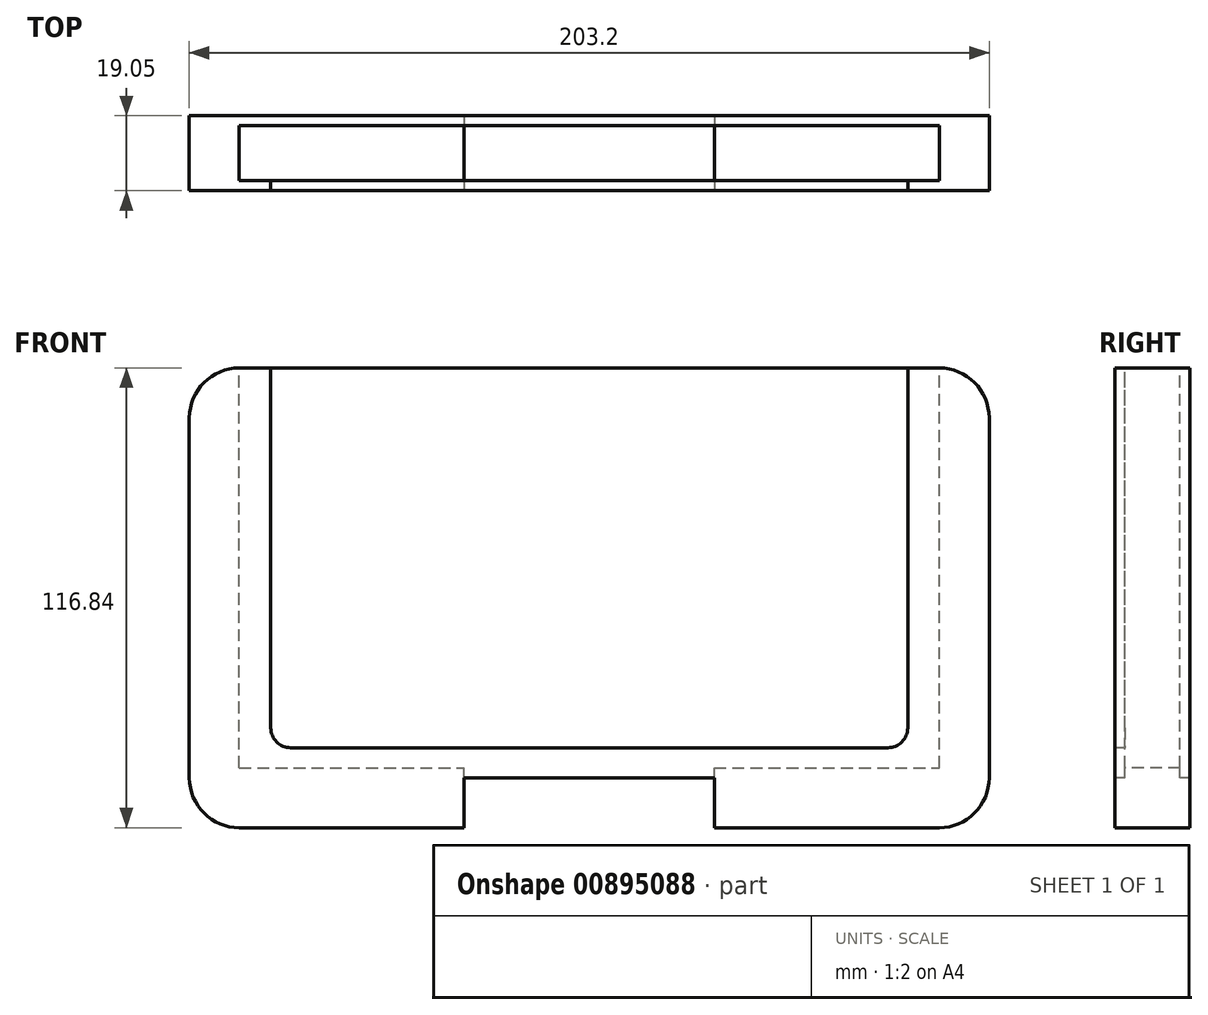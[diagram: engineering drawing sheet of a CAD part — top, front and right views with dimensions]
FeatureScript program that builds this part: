
annotation { "Feature Type Name" : "Feature", "Feature Type Description" : "" }
export const myFeature = defineFeature(function(context is Context, id is Id, definition is map)
    precondition{}
    {
        {
            var Q0;
            Q0=qCreatedBy(makeId("Front.planeOp"),FACE);
            var sketch = newSketch(context, id + "F0", { "sketchPlane" : qUnion([Q0])});
            skLineSegment(sketch, "E0.bottom", {"start": v(0, 0) * mm, "end": v(203.2, 0) * mm});
            skLineSegment(sketch, "E0.top", {"start": v(0, 116.84) * mm, "end": v(203.2, 116.84) * mm});
            skLineSegment(sketch, "E0.left", {"start": v(0, 0) * mm, "end": v(0, 116.84) * mm});
            skLineSegment(sketch, "E0.right", {"start": v(203.2, 0) * mm, "end": v(203.2, 116.84) * mm});
            skSolve(sketch);
        }
        {
            var Q0;
            Q0=makeQuery(id+"F0.imprint","IMPRINT",FACE,{"disambiguationData":[TD([[makeQuery(id+"F0.imprint","IMPRINT",EDGE,{"derivedFrom":sQuery(id+"F0.wireOp",EDGE,"E0.bottom")}),1.0]])]});
            extrude(context, id + "F1", {"entities" : qUnion([Q0]), "depth" : 19.05 * mm, "offsetDistance" : 25.4 * mm});
        }
        {
            var Q0;
            Q0=makeQuery(id+"F1.opExtrude","SWEPT_FACE",FACE,{"disambiguationData":[OSD([sQuery(id+"F0.wireOp",EDGE,"E0.top")])]});
            var sketch = newSketch(context, id + "F2", { "sketchPlane" : qUnion([Q0])});
            skLineSegment(sketch, "E1.bottom", {"start": v(12.7, -2.54) * mm, "end": v(190.5, -2.54) * mm});
            skLineSegment(sketch, "E1.top", {"start": v(12.7, -16.51) * mm, "end": v(190.5, -16.51) * mm});
            skLineSegment(sketch, "E1.left", {"start": v(12.7, -2.54) * mm, "end": v(12.7, -16.51) * mm});
            skLineSegment(sketch, "E1.right", {"start": v(190.5, -2.54) * mm, "end": v(190.5, -16.5) * mm});
            skLineSegment(sketch, "E2", {"start": v(101.6, 16.65) * mm, "end": v(101.6, -49.67) * mm, "construction": true});
            skPoint(sketch, "E3", {"position": v(101.6, -16.51) * mm});
            skSolve(sketch);
        }
        {
            var Q0;
            {var subQ0=sQuery(id+"F2.wireOp",EDGE,"E1.bottom");var subQ1=sQuery(id+"F0.wireOp",EDGE,"E0.top");var subQ2=makeQuery(id+"F1.opExtrude","SWEPT_EDGE",EDGE,{"disambiguationData":[OSD([subQ1,sQuery(id+"F0.wireOp",EDGE,"E0.left")])]});var subQ3=makeQuery(id+"F2.imprint","INTERSECT",VERTEX,{"derivedFrom":[subQ2,subQ0]});Q0=makeQuery(id+"F2.imprint","IMPRINT",FACE,{"disambiguationData":[TD([[makeQuery(id+"F2.imprint","IMPRINT",EDGE,{"disambiguationData":[TD([[subQ3,-1.0]])],"derivedFrom":subQ0}),-1.0]])]});}
            extrude(context, id + "F3", {"entities" : qUnion([Q0]), "operationType" : NewBodyOperationType.REMOVE, "oppositeDirection" : true, "depth" : 101.6 * mm, "offsetDistance" : 25.4 * mm});
        }
        {
            var Q0;
            Q0=makeQuery(id+"F1.opExtrude","CAP_FACE",FACE,{"disambiguationData":[OSD([sQuery(id+"F0.wireOp",EDGE,"E0.bottom"),sQuery(id+"F0.wireOp",EDGE,"E0.top"),sQuery(id+"F0.wireOp",EDGE,"E0.left"),sQuery(id+"F0.wireOp",EDGE,"E0.right")])],"isStart":false});
            var sketch = newSketch(context, id + "F4", { "sketchPlane" : qUnion([Q0])});
            skLineSegment(sketch, "E4.bottom", {"start": v(20.7, 116.84) * mm, "end": v(182.5, 116.84) * mm});
            skLineSegment(sketch, "E4.top", {"start": v(20.7, 20.32) * mm, "end": v(182.5, 20.32) * mm});
            skLineSegment(sketch, "E4.left", {"start": v(20.7, 116.84) * mm, "end": v(20.7, 20.32) * mm});
            skLineSegment(sketch, "E4.right", {"start": v(182.5, 116.84) * mm, "end": v(182.5, 20.32) * mm});
            skLineSegment(sketch, "E5", {"start": v(20.7, 116.84) * mm, "end": v(182.5, 20.32) * mm, "construction": true});
            skLineSegment(sketch, "E6", {"start": v(101.6, 20.32) * mm, "end": v(101.6, 213.36) * mm, "construction": true});
            skPoint(sketch, "E7.0", {"position": v(101.6, 116.84) * mm});
            skSolve(sketch);
        }
        {
            var Q0;
            Q0=makeQuery(id+"F4.imprint","IMPRINT",FACE,{"disambiguationData":[TD([[makeQuery(id+"F4.imprint","IMPRINT",EDGE,{"derivedFrom":sQuery(id+"F4.wireOp",EDGE,"E4.bottom")}),-1.0]])]});
            extrude(context, id + "F5", {"entities" : qUnion([Q0]), "operationType" : NewBodyOperationType.REMOVE, "endBound" : BoundingType.UP_TO_NEXT, "oppositeDirection" : true, "depth" : 25.4 * mm, "offsetDistance" : 25.4 * mm});
        }
        {
            var Q0;
            Q0=makeQuery(id+"F3.boolean.opBoolean","COPY",FACE,{"derivedFrom":makeQuery(id+"F3.opExtrude","CAP_FACE",FACE,{"disambiguationData":[OSD([sQuery(id+"F0.wireOp",EDGE,"E0.top"),sQuery(id+"F0.wireOp",EDGE,"E0.left"),sQuery(id+"F0.wireOp",EDGE,"E0.right"),sQuery(id+"F2.wireOp",EDGE,"E1.bottom"),sQuery(id+"F2.wireOp",EDGE,"E1.top")])],"isStart":false})});
            var sketch = newSketch(context, id + "F6", { "sketchPlane" : qUnion([Q0])});
            skLineSegment(sketch, "E8", {"start": v(101.6, 50.21) * mm, "end": v(101.6, -50.21) * mm, "construction": true});
            skLineSegment(sketch, "E9", {"start": v(6.81, -9.53) * mm, "end": v(369.1, -9.52) * mm, "construction": true});
            skPoint(sketch, "E10", {"position": v(101.6, -9.53) * mm});
            skLineSegment(sketch, "E11.bottom", {"start": v(133.35, -2.54) * mm, "end": v(69.85, -2.54) * mm});
            skLineSegment(sketch, "E11.top", {"start": v(133.35, -16.5) * mm, "end": v(69.85, -16.5) * mm});
            skLineSegment(sketch, "E11.left", {"start": v(133.35, -2.54) * mm, "end": v(133.35, -16.5) * mm});
            skLineSegment(sketch, "E11.right", {"start": v(69.85, -2.54) * mm, "end": v(69.85, -16.5) * mm});
            skSolve(sketch);
        }
        {
            var Q0;
            Q0=makeQuery(id+"F6.imprint","IMPRINT",FACE,{"disambiguationData":[TD([[makeQuery(id+"F6.imprint","IMPRINT",EDGE,{"derivedFrom":sQuery(id+"F6.wireOp",EDGE,"E11.bottom")}),-1.0]])]});
            extrude(context, id + "F7", {"entities" : qUnion([Q0]), "operationType" : NewBodyOperationType.REMOVE, "endBound" : BoundingType.THROUGH_ALL, "oppositeDirection" : true, "depth" : 25.4 * mm, "offsetDistance" : 25.4 * mm});
        }
        {
            var Q0;
            Q0=makeQuery(id+"F1.opExtrude","CAP_FACE",FACE,{"disambiguationData":[OSD([sQuery(id+"F0.wireOp",EDGE,"E0.bottom"),sQuery(id+"F0.wireOp",EDGE,"E0.top"),sQuery(id+"F0.wireOp",EDGE,"E0.left"),sQuery(id+"F0.wireOp",EDGE,"E0.right")])],"isStart":false});
            var sketch = newSketch(context, id + "F8", { "sketchPlane" : qUnion([Q0])});
            skLineSegment(sketch, "E12", {"start": v(101.6, 241.75) * mm, "end": v(101.6, -8.07) * mm, "construction": true});
            skPoint(sketch, "E13.0", {"position": v(69.85, 0) * mm});
            skPoint(sketch, "E14.0", {"position": v(133.35, 0) * mm});
            skLineSegment(sketch, "E15.bottom", {"start": v(69.85, 0) * mm, "end": v(133.35, 0) * mm});
            skLineSegment(sketch, "E15.top", {"start": v(69.85, 12.7) * mm, "end": v(133.35, 12.7) * mm});
            skLineSegment(sketch, "E15.left", {"start": v(69.85, 0) * mm, "end": v(69.85, 12.7) * mm});
            skLineSegment(sketch, "E15.right", {"start": v(133.35, 0) * mm, "end": v(133.35, 12.7) * mm});
            skSolve(sketch);
        }
        {
            var Q0;
            Q0=makeQuery(id+"F8.imprint","IMPRINT",FACE,{"disambiguationData":[TD([[makeQuery(id+"F8.imprint","IMPRINT",EDGE,{"derivedFrom":sQuery(id+"F8.wireOp",EDGE,"E15.bottom")}),1.0]])]});
            extrude(context, id + "F9", {"entities" : qUnion([Q0]), "operationType" : NewBodyOperationType.REMOVE, "endBound" : BoundingType.THROUGH_ALL, "oppositeDirection" : true, "depth" : 25.4 * mm, "offsetDistance" : 25.4 * mm});
        }
        {
            var Q0;
            Q0=makeQuery(id+"F1.opExtrude","SWEPT_EDGE",EDGE,{"disambiguationData":[OSD([sQuery(id+"F0.wireOp",EDGE,"E0.top"),sQuery(id+"F0.wireOp",EDGE,"E0.left")])]});
            var Q1;
            Q1=makeQuery(id+"F1.opExtrude","SWEPT_EDGE",EDGE,{"disambiguationData":[OSD([sQuery(id+"F0.wireOp",EDGE,"E0.bottom"),sQuery(id+"F0.wireOp",EDGE,"E0.left")])]});
            var Q2;
            Q2=makeQuery(id+"F1.opExtrude","SWEPT_EDGE",EDGE,{"disambiguationData":[OSD([sQuery(id+"F0.wireOp",EDGE,"E0.bottom"),sQuery(id+"F0.wireOp",EDGE,"E0.right")])]});
            var Q3;
            Q3=makeQuery(id+"F1.opExtrude","SWEPT_EDGE",EDGE,{"disambiguationData":[OSD([sQuery(id+"F0.wireOp",EDGE,"E0.top"),sQuery(id+"F0.wireOp",EDGE,"E0.right")])]});
            fillet(context, id + "F10", {"entities" : qUnion([Q0, Q1, Q2, Q3]), "radius" : 12.7 * mm, "tangentPropagation" : true, "allowEdgeOverflow" : false});
        }
        {
            var Q0;
            Q0=makeQuery(id+"F5.boolean.opBoolean","COPY",EDGE,{"derivedFrom":makeQuery(id+"F5.opExtrude","SWEPT_EDGE",EDGE,{"disambiguationData":[OSD([sQuery(id+"F4.wireOp",EDGE,"E4.top"),sQuery(id+"F4.wireOp",EDGE,"E4.left")])]})});
            var Q1;
            Q1=makeQuery(id+"F5.boolean.opBoolean","COPY",EDGE,{"derivedFrom":makeQuery(id+"F5.opExtrude","SWEPT_EDGE",EDGE,{"disambiguationData":[OSD([sQuery(id+"F4.wireOp",EDGE,"E4.top"),sQuery(id+"F4.wireOp",EDGE,"E4.right")])]})});
            fillet(context, id + "F11", {"entities" : qUnion([Q0, Q1]), "radius" : 5.08 * mm, "tangentPropagation" : true, "allowEdgeOverflow" : false});
        }
    });
